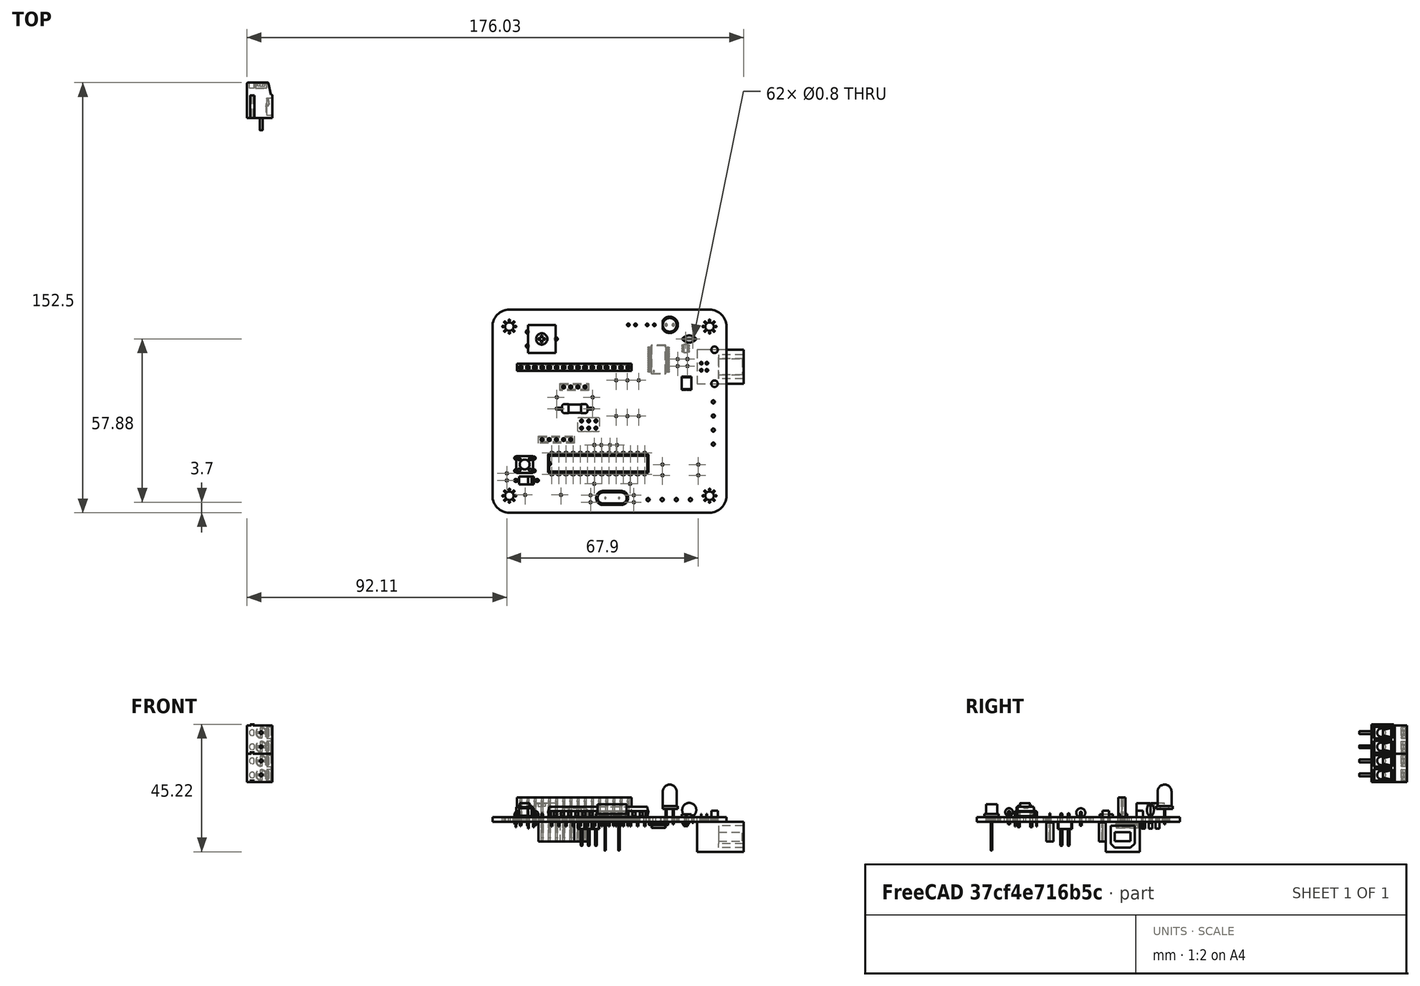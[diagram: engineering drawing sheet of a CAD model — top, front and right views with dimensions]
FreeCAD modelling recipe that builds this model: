
FCSTD DOCUMENT  (FreeCAD 0.19R22665 (Git))
Label: pcb_board
License: All rights reserved
LicenseURL: http://en.wikipedia.org/wiki/All_rights_reserved
objects: App::Link×20, Part::Feature×19, App::Part×6, PartDesign::CoordinateSystem×4, Sketcher::SketchObject×1
note: 24 computed .brp shape members not serialized (recipe doc carries the construction recipe); baked Part::Feature solids carry a one-line shape summary decoded from their .brp

FEATURE [PartDesign::CoordinateSystem] Local_CS_8929
  AttacherType = Attacher::AttachEngine3D
FEATURE [Part::Feature] Pcb_8929
  shape: bbox 83 x 72 x 1.6 mm, 170 faces (baked)
FEATURE [Sketcher::SketchObject] PCB_Sketch_8929
  sketch-geometry (8):
    g0: LineSegment StartX=93 StartY=-68 StartZ=0 EndX=164 EndY=-68 EndZ=0
    g1: LineSegment StartX=170 StartY=-134 StartZ=0 EndX=170 EndY=-74 EndZ=0
    g2: LineSegment StartX=93 StartY=-140 StartZ=0 EndX=164 EndY=-140 EndZ=0
    g3: LineSegment StartX=87 StartY=-74 StartZ=0 EndX=87 EndY=-134 EndZ=0
    g4: ArcOfCircle CenterX=164 CenterY=-74 CenterZ=0 NormalX=0 NormalY=0 NormalZ=1 AngleXU=0 Radius=6 StartAngle=0 EndAngle=1.5708
    g5: ArcOfCircle CenterX=93 CenterY=-134 CenterZ=0 NormalX=0 NormalY=0 NormalZ=1 AngleXU=0 Radius=6 StartAngle=3.14159 EndAngle=4.71239
    g6: ArcOfCircle CenterX=164 CenterY=-134 CenterZ=0 NormalX=0 NormalY=0 NormalZ=1 AngleXU=0 Radius=6 StartAngle=4.71239 EndAngle=6.28319
    g7: ArcOfCircle CenterX=93 CenterY=-74 CenterZ=0 NormalX=0 NormalY=0 NormalZ=1 AngleXU=0 Radius=6 StartAngle=1.5708 EndAngle=3.14159
  constraints (8):
    c: Coincident(g3,g5)
    c: Coincident(g3,g7)
    c: Coincident(g2,g5)
    c: Coincident(g0,g7)
    c: Coincident(g2,g6)
    c: Coincident(g0,g4)
    c: Coincident(g1,g6)
    c: Coincident(g1,g4)
FEATURE [App::Part] Board_Geoms_8929
  Group = -> [Local_CS_8929,Pcb_8929,PCB_Sketch_8929]
  Origin = -> Origin
FEATURE [Part::Feature] Shape  label="J6_PinSocket_1x04_P254mm_Vertical_5FCA8662"
  Placement = pos=(112.235,-95.42,-1.6) rot=(0.707107,-0.707107,0;3.14159rad)
  shape: bbox 10.16 x 2.54 x 10.1 mm, 134 faces (baked)
FEATURE [Part::Feature] Shape001  label="SW1_SW_PUSH_6mm_h5mm_5FCE63C8"
  Placement = pos=(95.29,-120.64,0) rot=(0,0,1;0rad)
  shape: bbox 7.174 x 6 x 8.5 mm, 105 faces (baked)
FEATURE [Part::Feature] Shape002  label="J7_PinSocket_1x05_P254mm_Vertical_5FC31174"
  Placement = pos=(114.78,-114.07,-1.6) rot=(0.707107,0.707107,0;3.14159rad)
  shape: bbox 12.7 x 2.54 x 10.1 mm, 165 faces (baked)
FEATURE [Part::Feature] Shape003  label="RV1_ACP470_5F3BE09B"
  Placement = pos=(104.5,-78.4,0) rot=(0,0,-1;1.5708rad)
  shape: bbox 9.8 x 10 x 9 mm, 36 faces (baked)
FEATURE [App::Link] RV1_ACP470_5F3BE09B_ln_  label="RV1_ACP470_5F3BE09B[2]"
  LinkPlacement = pos=(104.5,-78.4,0) rot=(0,0,-1;1.5708rad)
  LinkedObject = -> Shape003
  Placement = pos=(104.5,-78.4,0) rot=(0,0,-1;1.5708rad)
FEATURE [Part::Feature] Shape004  label="D4_LED_D5.0mm_5FA6C0E4"
  Placement = pos=(148.6,-73.4,0) rot=(0,0,1;0rad)
  shape: bbox 5.4 x 5.8 x 14.1 mm, 16 faces (baked)
FEATURE [Part::Feature] Shape005  label="F1_MF-MSMF050_5FB19120[2]"
  Placement = pos=(155.79,-94.15,0) rot=(0,0,1;1.5708rad)
  shape: bbox 3.41 x 4.73 x 1.1 mm, 14 faces (baked)
FEATURE [App::Link] F1_MF_MSMF050_5FB19120_2__ln_  label="F1_MF-MSMF050_5FB19120[3]"
  LinkPlacement = pos=(155.79,-94.15,0) rot=(0,0,1;1.5708rad)
  LinkedObject = -> Shape005
  Placement = pos=(155.79,-94.15,0) rot=(0,0,1;1.5708rad)
FEATURE [Part::Feature] Shape006  label="U3_SOT_23_6_5FB065DB"
  Placement = pos=(155.53,-81.77,-1.6) rot=(0,1,0;3.14159rad)
  shape: bbox 2.8 x 2.9 x 1.55 mm, 124 faces (baked)
FEATURE [Part::Feature] Shape007  label="D3_D_DO-41_SOD81_P7.62mm_Horizontal_5FCE6338"
  Placement = pos=(102.89,-128.56,0) rot=(0,0,1;3.14159rad)
  shape: bbox 8.618 x 2.72 x 5.71 mm, 15 faces (baked)
FEATURE [Part::Feature] Shape008  label="C5_C_Disc_D50mm_W25mm_P250mm_5FB07593"
  Placement = pos=(158.04,-78.42,0) rot=(0,0,1;3.14159rad)
  shape: bbox 5 x 2.5 x 7.1 mm, 6 faces (baked)
FEATURE [Part::Feature] Part__Feature  label="TB001-500-02P_Green - P"
  shape: bbox 9 x 16.9 x 10.5 mm, 145 faces (baked)
FEATURE [Part::Feature] Part__Feature001  label="TB001-500-02P_Green - P001"
  Placement = pos=(0,0,10) rot=(0,0,1;0rad)
  shape: bbox 9 x 16.9 x 10.5 mm, 145 faces (baked)
FEATURE [App::Part] CUI_DEVICES_TB001_500_P04GR  label="J2_CUI_DEVICES_TB001-500-P04GR_5FCB9D5E[2]"
  Group = -> [Part__Feature,Part__Feature001]
  Origin = -> Origin008
  Placement = pos=(127.21,-130.36,-1.6) rot=(-0.57735,0.57735,-0.57735;2.0944rad)
FEATURE [App::Link] J2_CUI_DEVICES_TB001_500_P04GR_5FCB9D5E_2__ln_  label="J4_CUI_DEVICES_TB001-500-P04GR_5FA8521F[2]"
  LinkPlacement = pos=(160.325,-130.7,-1.6) rot=(-1,0,0;1.5708rad)
  LinkedObject = -> CUI_DEVICES_TB001_500_P04GR
  Placement = pos=(160.325,-130.7,-1.6) rot=(-1,0,0;1.5708rad)
FEATURE [Part::Feature] Shape009  label="J1_usb_b_conn_5FA8DFDA[2]"
  Placement = pos=(161.05,-89.5,-1.6) rot=(1,0,0;3.14159rad)
  shape: bbox 16.5 x 14.34 x 14.52 mm, 44 faces (baked)
FEATURE [Part::Feature] Shape010  label="U1_SSOP_28_53x102mm_P065mm_5FB0862F"
  Placement = pos=(145.91,-85.68,-1.6) rot=(1,0,0;3.14159rad)
  shape: bbox 7.8 x 10.2 x 2.1 mm, 456 faces (baked)
FEATURE [Part::Feature] Shape011  label="Y1_Crystal_5F93F8CD"
  Placement = pos=(129.46,-134.77,0) rot=(0,0,1;3.14159rad)
  shape: bbox 11.35 x 5 x 16.4 mm, 15 faces (baked)
FEATURE [Part::Feature] Shape012  label="U2_DIP-28_W7.62mm_5F8B1761"
  Placement = pos=(108,-126.4,0) rot=(0,0,1;1.5708rad)
  shape: bbox 35.56 x 7.874 x 6.98 mm, 488 faces (baked)
FEATURE [Part::Feature] Shape013  label="J3_PinSocket_1x16_P254mm_Vertical_5FB99047"
  Placement = pos=(97,-88.5,0) rot=(0,0,1;1.5708rad)
  shape: bbox 40.64 x 2.54 x 10.1 mm, 506 faces (baked)
FEATURE [Part::Feature] Shape014  label="J5_PinHeader_2x03_P254mm_Vertical_5FA86B0F"
  Placement = pos=(123.69,-110.005,-1.6) rot=(0.707107,0.707107,0;3.14159rad)
  shape: bbox 7.62 x 5.08 x 11.54 mm, 130 faces (baked)
FEATURE [App::Part] Bot_8929
  Group = -> [Shape,Shape002,Shape006,CUI_DEVICES_TB001_500_P04GR,J2_CUI_DEVICES_TB001_500_P04GR_5FCB9D5E_2__ln_,Shape009,Shape010,Shape014]
  Origin = -> Origin004
FEATURE [App::Link] C5_C_Disc_D50mm_W25mm_P250mm_5FB07593_ln_  label="C1_C_Disc_D50mm_W25mm_P250mm_5FA6C044"
  LinkPlacement = pos=(156.15,-88.02,0) rot=(0,0,1;1.5708rad)
  LinkedObject = -> Shape008
  Placement = pos=(156.15,-88.02,0) rot=(0,0,1;1.5708rad)
FEATURE [App::Link] C5_C_Disc_D50mm_W25mm_P250mm_5FB07593_ln_001  label="C2_C_Disc_D50mm_W25mm_P250mm_5FAFE4E7"
  LinkPlacement = pos=(152.68,-85.53,0) rot=(0,0,-1;1.5708rad)
  LinkedObject = -> Shape008
  Placement = pos=(152.68,-85.53,0) rot=(0,0,-1;1.5708rad)
FEATURE [App::Link] C5_C_Disc_D50mm_W25mm_P250mm_5FB07593_ln_002  label="C3_C_Disc_D50mm_W25mm_P250mm_5FA6C068"
  LinkPlacement = pos=(125.62,-116,0) rot=(0,0,1;3.14159rad)
  LinkedObject = -> Shape008
  Placement = pos=(125.62,-116,0) rot=(0,0,1;3.14159rad)
FEATURE [App::Link] C5_C_Disc_D50mm_W25mm_P250mm_5FB07593_ln_003  label="C4_C_Disc_D50mm_W25mm_P250mm_5FCE6386"
  LinkPlacement = pos=(92.11,-128.56,0) rot=(0,0,1;1.5708rad)
  LinkedObject = -> Shape008
  Placement = pos=(92.11,-128.56,0) rot=(0,0,1;1.5708rad)
FEATURE [App::Link] C5_C_Disc_D50mm_W25mm_P250mm_5FB07593_ln_004  label="C6_C_Disc_D50mm_W25mm_P250mm_5FA6D61D"
  LinkPlacement = pos=(128.67,-116,0) rot=(0,0,1;0rad)
  LinkedObject = -> Shape008
  Placement = pos=(128.67,-116,0) rot=(0,0,1;0rad)
FEATURE [App::Link] C5_C_Disc_D50mm_W25mm_P250mm_5FB07593_ln_005  label="C7_C_Disc_D50mm_W25mm_P250mm_5FA6C09E"
  LinkPlacement = pos=(121.8,-136.3,0) rot=(0,0,1;1.5708rad)
  LinkedObject = -> Shape008
  Placement = pos=(121.8,-136.3,0) rot=(0,0,1;1.5708rad)
FEATURE [App::Link] C5_C_Disc_D50mm_W25mm_P250mm_5FB07593_ln_006  label="C8_C_Disc_D50mm_W25mm_P250mm_5FA6C0B0"
  LinkPlacement = pos=(137.15,-136.3,0) rot=(0,0,1;1.5708rad)
  LinkedObject = -> Shape008
  Placement = pos=(137.15,-136.3,0) rot=(0,0,1;1.5708rad)
FEATURE [App::Link] D4_LED_D5_0mm_5FA6C0E4_ln_  label="D1_LED_D5.0mm_5FCBACB3"
  LinkPlacement = pos=(135.2,-73.4,0) rot=(0,0,1;0rad)
  LinkedObject = -> Shape004
  Placement = pos=(135.2,-73.4,0) rot=(0,0,1;0rad)
FEATURE [App::Link] D4_LED_D5_0mm_5FA6C0E4_ln_001  label="D2_LED_D5.0mm_5FCBAF12"
  LinkPlacement = pos=(141.9,-73.4,0) rot=(0,0,1;0rad)
  LinkedObject = -> Shape004
  Placement = pos=(141.9,-73.4,0) rot=(0,0,1;0rad)
FEATURE [Part::Feature] Shape015  label="R1_R_Axial_DIN0309_L90mm_D32mm_P1270mm_Horizontal_5FCA8AFD"
  Placement = pos=(109.85,-103.11,0) rot=(0,0,1;0rad)
  shape: bbox 13.63 x 3.464 x 6.332 mm, 17 faces (baked)
FEATURE [App::Link] R1_R_Axial_DIN0309_L90mm_D32mm_P1270mm_Horizontal_5FCA8AFD_ln_  label="R2_R_Axial_DIN0309_L90mm_D32mm_P1270mm_Horizontal_5FCA8ABB"
  LinkPlacement = pos=(109.85,-99.065,0) rot=(0,0,1;0rad)
  LinkedObject = -> Shape015
  Placement = pos=(109.85,-99.065,0) rot=(0,0,1;0rad)
FEATURE [App::Link] R1_R_Axial_DIN0309_L90mm_D32mm_P1270mm_Horizontal_5FCA8AFD_ln_001  label="R3_R_Axial_DIN0309_L90mm_D32mm_P1270mm_Horizontal_5FB070BF"
  LinkPlacement = pos=(130.875,-105.765,0) rot=(0,0,1;1.5708rad)
  LinkedObject = -> Shape015
  Placement = pos=(130.875,-105.765,0) rot=(0,0,1;1.5708rad)
FEATURE [App::Link] R1_R_Axial_DIN0309_L90mm_D32mm_P1270mm_Horizontal_5FCA8AFD_ln_002  label="R4_R_Axial_DIN0309_L90mm_D32mm_P1270mm_Horizontal_5FB0707D"
  LinkPlacement = pos=(134.875,-105.765,0) rot=(0,0,1;1.5708rad)
  LinkedObject = -> Shape015
  Placement = pos=(134.875,-105.765,0) rot=(0,0,1;1.5708rad)
FEATURE [App::Link] R1_R_Axial_DIN0309_L90mm_D32mm_P1270mm_Horizontal_5FCA8AFD_ln_003  label="R6_R_Axial_DIN0309_L90mm_D32mm_P1270mm_Horizontal_5FA6C1B1"
  LinkPlacement = pos=(111.3,-133.7,0) rot=(0,0,1;3.14159rad)
  LinkedObject = -> Shape015
  Placement = pos=(111.3,-133.7,0) rot=(0,0,1;3.14159rad)
FEATURE [App::Link] R1_R_Axial_DIN0309_L90mm_D32mm_P1270mm_Horizontal_5FCA8AFD_ln_004  label="R7_R_Axial_DIN0309_L90mm_D32mm_P1270mm_Horizontal_5FA6CB65"
  LinkPlacement = pos=(123.1,-129.75,0) rot=(0,0,1;0rad)
  LinkedObject = -> Shape015
  Placement = pos=(123.1,-129.75,0) rot=(0,0,1;0rad)
FEATURE [App::Link] R1_R_Axial_DIN0309_L90mm_D32mm_P1270mm_Horizontal_5FCA8AFD_ln_005  label="R8_R_Axial_DIN0309_L90mm_D32mm_P1270mm_Horizontal_5FA6F1A2"
  LinkPlacement = pos=(147.31,-122.925,0) rot=(0,0,1;0rad)
  LinkedObject = -> Shape015
  Placement = pos=(147.31,-122.925,0) rot=(0,0,1;0rad)
FEATURE [App::Link] R1_R_Axial_DIN0309_L90mm_D32mm_P1270mm_Horizontal_5FCA8AFD_ln_006  label="R9_R_Axial_DIN0309_L90mm_D32mm_P1270mm_Horizontal_5FB07101"
  LinkPlacement = pos=(138.875,-93.065,0) rot=(0,0,-1;1.5708rad)
  LinkedObject = -> Shape015
  Placement = pos=(138.875,-93.065,0) rot=(0,0,-1;1.5708rad)
FEATURE [App::Link] R1_R_Axial_DIN0309_L90mm_D32mm_P1270mm_Horizontal_5FCA8AFD_ln_007  label="R11_R_Axial_DIN0309_L90mm_D32mm_P1270mm_Horizontal_5FCB9A34"
  LinkPlacement = pos=(160.01,-126.73,0) rot=(0,0,1;3.14159rad)
  LinkedObject = -> Shape015
  Placement = pos=(160.01,-126.73,0) rot=(0,0,1;3.14159rad)
FEATURE [App::Part] Top_8929
  Group = -> [Shape001,Shape003,RV1_ACP470_5F3BE09B_ln_,Shape004,Shape005,F1_MF_MSMF050_5FB19120_2__ln_,Shape007,Shape008,Shape011,Shape012,Shape013,C5_C_Disc_D50mm_W25mm_P250mm_5FB07593_ln_,C5_C_Disc_D50mm_W25mm_P250mm_5FB07593_ln_001,C5_C_Disc_D50mm_W25mm_P250mm_5FB07593_ln_002,C5_C_Disc_D50mm_W25mm_P250mm_5FB07593_ln_003,C5_C_Disc_D50mm_W25mm_P250mm_5FB07593_ln_004,+13 more]
  Origin = -> Origin003
FEATURE [App::Part] Step_Models_8929
  Group = -> [Top_8929,Bot_8929]
  Origin = -> Origin002
FEATURE [PartDesign::CoordinateSystem] LCS_lcd
  AttacherType = Attacher::AttachEngine3D
  MapMode = 7
  Placement = pos=(95.73,-87.23,7) rot=(0,0.707107,0.707107;3.14159rad)
  Support = -> [Shape013]
FEATURE [PartDesign::CoordinateSystem] LCS_box
  AttacherType = Attacher::AttachEngine3D
  MapMode = 11
  Placement = pos=(93,-134,-1.6) rot=(0,0,1;1.5708rad)
  Support = -> [Pcb_8929]
FEATURE [PartDesign::CoordinateSystem] LCS_exp
  AttacherType = Attacher::AttachEngine3D
  MapMode = 45
  Placement = pos=(104.62,-114.07,-2.85) rot=(0,0,1;1.5708rad)
  Support = -> [Shape002]
FEATURE [App::Part] Board_8929  label="livello_serbatoio_definitiva"
  Group = -> [Board_Geoms_8929,Step_Models_8929,LCS_lcd,LCS_box,LCS_exp]
  Origin = -> Origin001
